# Revit family: Camera-Security-Vaddio-PTZ-RoboShot
name_source: partatom
category: Communication Devices
revit_build: Autodesk Revit 2015 (Build: 20140905_0730(x64)
units: mm (PartAtom-declared; Revit-internal decimal feet)

## types (105) — shared parameters
Date Modified = February 28, 2019
Default Elevation = 48 "
Description = See Part Description
Equipment Abbreviation = SC
Family Version = 1.0
Manufacturer = Vaddio
Model = See Part Number
Model Disclaimer = Contact Vaddio For More Information
Mount Material = Steel - Vaddio - White
Mount Trim Material = Plastic - Vaddio - White
Product Page URL = http://www.vaddio.com
URL = http://www.vaddio.com

## per-type parameters (varying)
| type | Camera Material | Camera Trim Material | Humidity | Image Sensor | Lens Type | Product Documentation Link | Resolution | Sales Region | Signal to Noise Ratio | Storage Temperature | Wide Dynamic Range | z Part Description | z Part Number | z Type Camera Series | z Type Mount Series |
| AVBMP, 12x Zoom, North America, Silver | Plastic - Vaddio - Silver | Plastic - Vaddio - Black | 20% to 80% Humidity | Exmor 1/2.8?, 2.34 Megapixel, Full HD (1080p/60 native) High-speed, Low Noise CMOS Image Sensor | 12X Optical Zoom with 73.0ø (wide end) to 6.6ø (tele end), f=3.91mm to 47mm, F1.8 to F3.4 | http://www.vaddio.com | 1080 x 1920 | North America | > 50 dB | 0øC to +40øC (32øF to 104øF) | No | Vaddio AVBMP, 12x Zoom, North America, Silver PTZ Camera | 999-9900-500 | 12 | 30 |
| AVBMP, 30x Zoom, North America, Black | Plastic - Vaddio - Black | Plastic - Vaddio - Black | 20% to 80% Humidity | Exmor 1/2.8?, 2.38 Megapixel, Full HD (1080p/60 native) High-speed, Low Noise CMOS Image Sensor | 30X Optical Zoom | http://www.vaddio.com | 1080 x 1920 | North America | > 50 dB | 0øC to +40øC (32øF to 104øF) | No | Vaddio AVBMP, 30x Zoom, North America, Black PTZ Camera | 999-9910-500 | 30 | 30 |
| AVBMP, 30x Zoom, North America, White | Plastic - Vaddio - White | Plastic - Vaddio - White | 20% to 80% Humidity | Exmor 1/2.8?, 2.38 Megapixel, Full HD (1080p/60 native) High-speed, Low Noise CMOS Image Sensor | 30X Optical Zoom | http://www.vaddio.com | 1080 x 1920 | North America | > 50 dB | 0øC to +40øC (32øF to 104øF) | No | Vaddio AVBMP, 30x Zoom, North America, White PTZ Camera | 999-9910-500W | 30 | 30 |
| AVBMP, 12x Zoom, North America, Elite, Black | Plastic - Vaddio - Black | Plastic - Vaddio - Black | 20% to 80% Humidity | Exmor 1/2.8?, 2.34 Megapixel, Full HD (1080p/60 native) High-speed, Low Noise CMOS Image Sensor | 12X Optical Zoom with 73.0ø (wide end) to 6.6ø (tele end), f=3.91mm to 47mm, F1.8 to F3.4 |  | 1080 x 1920 | North America | > 50 dB | 0øC to +40øC (32øF to 104øF) | No | Vaddio AVBMP, 12x Zoom, North America, Elite, Black PTZ Camera | 999-99000-500 | 12 | 30 |
| AVBMP, 12x Zoom, North America, Elite, White | Plastic - Vaddio - White | Plastic - Vaddio - White | 20% to 80% Humidity | Exmor 1/2.8?, 2.34 Megapixel, Full HD (1080p/60 native) High-speed, Low Noise CMOS Image Sensor | 12X Optical Zoom with 73.0ø (wide end) to 6.6ø (tele end), f=3.91mm to 47mm, F1.8 to F3.4 |  | 1080 x 1920 | North America | > 50 dB | 0øC to +40øC (32øF to 104øF) | No | Vaddio AVBMP, 12x Zoom, North America, Elite, White PTZ Camera | 999-99000-500W | 12 | 30 |
| AVBMP, 30x Zoom, North America, Elite, Black | Plastic - Vaddio - Black | Plastic - Vaddio - Black | 20% to 80% Humidity | Exmor 1/2.8?, 2.38 Megapixel, Full HD (1080p/60 native) High-speed, Low Noise CMOS Image Sensor | 30X Optical Zoom |  | 1080 x 1920 | North America | > 50 dB | 0øC to +40øC (32øF to 104øF) | No | Vaddio AVBMP, 30x Zoom, North America, Elite, Black PTZ Camera | 999-99100-500 | 30 | 30 |
| AVBMP, 30x Zoom, North America, Elite, White | Plastic - Vaddio - White | Plastic - Vaddio - White | 20% to 80% Humidity | Exmor 1/2.8?, 2.38 Megapixel, Full HD (1080p/60 native) High-speed, Low Noise CMOS Image Sensor | 30X Optical Zoom |  | 1080 x 1920 | North America | > 50 dB | 0øC to +40øC (32øF to 104øF) | No | Vaddio AVBMP, 30x Zoom, North America, Elite, White PTZ Camera | 999-99100-500W | 30 | 30 |
| HDBT, 30x Zoom, North America, Black | Plastic - Vaddio - Black | Plastic - Vaddio - Black | 20% to 80% RH, non-condensing | 1/2.8-Type Exmor R? backlit CMOS sensor | 30X optical zoom, 65ø (wide) to 2.3ø (tele), F1.6 to F4.7 | http://www.vaddio.com | 1080 x 1920 | North America | More than 50 dB | 0øC to +40øC (32øF to 104øF) | No | Vaddio HDBT, 30x Zoom, North America, Black PTZ Camera | 999-9963-000 | 30 | 30 |
| HDBT, 30x Zoom, North America, White | Plastic - Vaddio - White | Plastic - Vaddio - White | 20% to 80% RH, non-condensing | 1/2.8-Type Exmor R? backlit CMOS sensor | 30X optical zoom, 65ø (wide) to 2.3ø (tele), F1.6 to F4.7 | http://www.vaddio.com | 1080 x 1920 | North America | More than 50 dB | 0øC to +40øC (32øF to 104øF) | No | Vaddio HDBT, 30x Zoom, North America, White PTZ Camera | 999-9963-000W | 30 | 30 |
| HDBT, 30x Zoom, Europe/UK, Black | Plastic - Vaddio - Black | Plastic - Vaddio - Black | 20% to 80% RH, non-condensing | 1/2.8-Type Exmor R? backlit CMOS sensor | 30X optical zoom, 65ø (wide) to 2.3ø (tele), F1.6 to F4.7 | http://www.vaddio.com | 1080 x 1920 | Europe/UK | More than 50 dB | 0øC to +40øC (32øF to 104øF) | No | Vaddio HDBT, 30x Zoom, Europe/UK, Black PTZ Camera | 999-9963-001 | 30 | 30 |
| HDBT, 30x Zoom, Europe/UK, White | Plastic - Vaddio - White | Plastic - Vaddio - White | 20% to 80% RH, non-condensing | 1/2.8-Type Exmor R? backlit CMOS sensor | 30X optical zoom, 65ø (wide) to 2.3ø (tele), F1.6 to F4.7 | http://www.vaddio.com | 1080 x 1920 | Europe/UK | More than 50 dB | 0øC to +40øC (32øF to 104øF) | No | Vaddio HDBT, 30x Zoom, Europe/UK, White PTZ Camera | 999-9963-001W | 30 | 30 |
| HDBT, 30x Zoom, Australia/New Zealand, Black | Plastic - Vaddio - Black | Plastic - Vaddio - Black | 20% to 80% RH, non-condensing | 1/2.8-Type Exmor R? backlit CMOS sensor | 30X optical zoom, 65ø (wide) to 2.3ø (tele), F1.6 to F4.7 | http://www.vaddio.com | 1080 x 1920 | Australia/New Zealand | More than 50 dB | 0øC to +40øC (32øF to 104øF) | No | Vaddio HDBT, 30x Zoom, Australia/New Zealand, Black PTZ Camera | 999-9963-009 | 30 | 30 |
| HDBT, 30x Zoom, Australia/New Zealand, White | Plastic - Vaddio - White | Plastic - Vaddio - White | 20% to 80% RH, non-condensing | 1/2.8-Type Exmor R? backlit CMOS sensor | 30X optical zoom, 65ø (wide) to 2.3ø (tele), F1.6 to F4.7 | http://www.vaddio.com | 1080 x 1920 | Australia/New Zealand | More than 50 dB | 0øC to +40øC (32øF to 104øF) | No | Vaddio HDBT, 30x Zoom, Australia/New Zealand, White PTZ Camera | 999-9963-009W | 30 | 30 |
| HDBT, 12x Zoom, North America, Silver | Plastic - Vaddio - Silver | Plastic - Vaddio - Black | 20% to 80% RH, non-condensing | 1/2.8-Type Exmor? CMOS sensor | 12X optical zoom, 73.0ø (wide) to 6.6ø (tele), f=3.91mm to 47.0mm,ÿ F1.8 to F3.4 | http://www.vaddio.com | 1080 x 1920 | North America | More than 50 dB | 0øC to +40øC (32øF to 104øF) | No | Vaddio HDBT, 12x Zoom, North America, Silver PTZ Camera | 999-9960-000 | 12 | 30 |
| HDBT, 12x Zoom, Europe/UK, Silver | Plastic - Vaddio - Silver | Plastic - Vaddio - Black | 20% to 80% RH, non-condensing | 1/2.8-Type Exmor? CMOS sensor | 12X optical zoom, 73.0ø (wide) to 6.6ø (tele), f=3.91mm to 47.0mm,ÿ F1.8 to F3.4 | http://www.vaddio.com | 1080 x 1920 | Europe/UK | More than 50 dB | 0øC to +40øC (32øF to 104øF) | No | Vaddio HDBT, 12x Zoom, Europe/UK, Silver PTZ Camera | 999-9960-001 | 12 | 30 |
| HDBT, 12x Zoom, Australia/New Zealand, Silver | Plastic - Vaddio - Silver | Plastic - Vaddio - Black | 20% to 80% RH, non-condensing | 1/2.8-Type Exmor? CMOS sensor | 12X optical zoom, 73.0ø (wide) to 6.6ø (tele), f=3.91mm to 47.0mm,ÿ F1.8 to F3.4 | http://www.vaddio.com | 1080 x 1920 | Australia/New Zealand | More than 50 dB | 0øC to +40øC (32øF to 104øF) | No | Vaddio HDBT, 12x Zoom, Australia/New Zealand, Silver PTZ Camera | 999-9960-009 | 12 | 30 |
| HDBT, 12x Zoom, North America, Elite, Black | Plastic - Vaddio - Black | Plastic - Vaddio - Black | 20% to 80% RH, non-condensing | 1/2.5 Type Exmor R CMOS Sensor | 12x optical zoom, f=4.4mm wide end to 88.4mm tele end, F2 to F3.8 | http://www.vaddio.com | 1080 x 1920 | North America | More than 50 dB | 0øC to +40øC (32øF to 104øF) | Yes | Vaddio HDBT, 12x Zoom, North America, Elite, Black PTZ Camera | 999-99600-000 | 12 | 30 |
| HDBT, 12x Zoom, North America, Elite, White | Plastic - Vaddio - White | Plastic - Vaddio - White | 20% to 80% RH, non-condensing | 1/2.5 Type Exmor R CMOS Sensor | 12x optical zoom, f=4.4mm wide end to 88.4mm tele end, F2 to F3.8 | http://www.vaddio.com | 1080 x 1920 | North America | More than 50 dB | 0øC to +40øC (32øF to 104øF) | Yes | Vaddio HDBT, 12x Zoom, North America, Elite, White PTZ Camera | 999-99600-000W | 12 | 30 |
| HDBT, 30x Zoom, North America, Elite, Black | Plastic - Vaddio - Black | Plastic - Vaddio - Black | 20% to 80% RH, non-condensing | 1/2.5 Type Exmor R CMOS Sensor | 30x zoom, 20 x optical zoom + 10x IntelliZoom, f=4.4mm wide end to 88.4mm tele end, F2 to F3.8 | http://www.vaddio.com | 1080 x 1920 | North America | More than 50 dB | 0øC to +40øC (32øF to 104øF) | Yes | Vaddio HDBT, 30x Zoom, North America, Elite, Black PTZ Camera | 999-99630-000 | 30 | 30 |
| HDBT, 30x Zoom, North America, Elite, White | Plastic - Vaddio - White | Plastic - Vaddio - White | 20% to 80% RH, non-condensing | 1/2.5 Type Exmor R CMOS Sensor | 30x zoom, 20 x optical zoom + 10x IntelliZoom, f=4.4mm wide end to 88.4mm tele end, F2 to F3.8 | http://www.vaddio.com | 1080 x 1920 | North America | More than 50 dB | 0øC to +40øC (32øF to 104øF) | Yes | Vaddio HDBT, 30x Zoom, North America, Elite, White PTZ Camera | 999-99630-000W | 30 | 30 |
| HDBT, 12x Zoom, Europe/UK, Elite, Black | Plastic - Vaddio - Black | Plastic - Vaddio - Black | 20% to 80% RH, non-condensing | 1/2.5 Type Exmor R CMOS Sensor | 12x optical zoom, f=4.4mm wide end to 88.4mm tele end, F2 to F3.8 | http://www.vaddio.com | 1080 x 1920 | Europe/UK | More than 50 dB | 0øC to +40øC (32øF to 104øF) | Yes | Vaddio HDBT, 12x Zoom, Europe/UK, Elite, Black PTZ Camera | 999-99600-001 | 12 | 30 |
| HDBT, 12x Zoom, Europe/UK, Elite, White | Plastic - Vaddio - White | Plastic - Vaddio - White | 20% to 80% RH, non-condensing | 1/2.5 Type Exmor R CMOS Sensor | 12x optical zoom, f=4.4mm wide end to 88.4mm tele end, F2 to F3.8 | http://www.vaddio.com | 1080 x 1920 | Europe/UK | More than 50 dB | 0øC to +40øC (32øF to 104øF) | Yes | Vaddio HDBT, 12x Zoom, Europe/UK, Elite, White PTZ Camera | 999-99600-001W | 12 | 30 |
| HDBT, 30x Zoom, Europe/UK, Elite, Black | Plastic - Vaddio - Black | Plastic - Vaddio - Black | 20% to 80% RH, non-condensing | 1/2.5 Type Exmor R CMOS Sensor | 30x zoom, 20 x optical zoom + 10x IntelliZoom, f=4.4mm wide end to 88.4mm tele end, F2 to F3.8 | http://www.vaddio.com | 1080 x 1920 | Europe/UK | More than 50 dB | 0øC to +40øC (32øF to 104øF) | Yes | Vaddio HDBT, 30x Zoom, Europe/UK, Elite, Black PTZ Camera | 999-99630-001 | 30 | 30 |
| HDBT, 30x Zoom, Europe/UK, Elite, White | Plastic - Vaddio - White | Plastic - Vaddio - White | 20% to 80% RH, non-condensing | 1/2.5 Type Exmor R CMOS Sensor | 30x zoom, 20 x optical zoom + 10x IntelliZoom, f=4.4mm wide end to 88.4mm tele end, F2 to F3.8 | http://www.vaddio.com | 1080 x 1920 | Europe/UK | More than 50 dB | 0øC to +40øC (32øF to 104øF) | Yes | Vaddio HDBT, 30x Zoom, Europe/UK, Elite, White PTZ Camera | 999-99630-001W | 30 | 30 |
| HDBT, 12x Zoom, Australia/New Zealand, Elite, Black | Plastic - Vaddio - Black | Plastic - Vaddio - Black | 20% to 80% RH, non-condensing | 1/2.5 Type Exmor R CMOS Sensor | 12x optical zoom, f=4.4mm wide end to 88.4mm tele end, F2 to F3.8 | http://www.vaddio.com | 1080 x 1920 | Australia/New Zealand | More than 50 dB | 0øC to +40øC (32øF to 104øF) | Yes | Vaddio HDBT, 12x Zoom, Australia/New Zealand, Elite, Black PTZ Camera | 999-99600-009 | 12 | 30 |
| HDBT, 12x Zoom, Australia/New Zealand, Elite, White | Plastic - Vaddio - White | Plastic - Vaddio - White | 20% to 80% RH, non-condensing | 1/2.5 Type Exmor R CMOS Sensor | 12x optical zoom, f=4.4mm wide end to 88.4mm tele end, F2 to F3.8 | http://www.vaddio.com | 1080 x 1920 | Australia/New Zealand | More than 50 dB | 0øC to +40øC (32øF to 104øF) | Yes | Vaddio HDBT, 12x Zoom, Australia/New Zealand, Elite, White PTZ Camera | 999-99600-009W | 12 | 30 |
| HDBT, 30x Zoom, Australia/New Zealand, Elite, Black | Plastic - Vaddio - Black | Plastic - Vaddio - Black | 20% to 80% RH, non-condensing | 1/2.5 Type Exmor R CMOS Sensor | 30x zoom, 20 x optical zoom + 10x IntelliZoom, f=4.4mm wide end to 88.4mm tele end, F2 to F3.8 | http://www.vaddio.com | 1080 x 1920 | Australia/New Zealand | More than 50 dB | 0øC to +40øC (32øF to 104øF) | Yes | Vaddio HDBT, 30x Zoom, Australia/New Zealand, Elite, Black PTZ Camera | 999-99630-009 | 30 | 30 |
| HDBT, 30x Zoom, Australia/New Zealand, Elite, White | Plastic - Vaddio - White | Plastic - Vaddio - White | 20% to 80% RH, non-condensing | 1/2.5 Type Exmor R CMOS Sensor | 30x zoom, 20 x optical zoom + 10x IntelliZoom, f=4.4mm wide end to 88.4mm tele end, F2 to F3.8 | http://www.vaddio.com | 1080 x 1920 | Australia/New Zealand | More than 50 dB | 0øC to +40øC (32øF to 104øF) | Yes | Vaddio HDBT, 30x Zoom, Australia/New Zealand, Elite, White PTZ Camera | 999-99630-009W | 30 | 30 |
| HDMI, 30x Zoom, North America, Black | Plastic - Vaddio - Black | Plastic - Vaddio - Black | 20% to 80% Humidity | Exmor 1/2.8?, 2.38 Megapixels, Full HD (1080p/60 native) High-speed, Low Noise CMOS Image Sensor | 65ø wide end to 2.3ø tele end, f=4.3mm to 129mm, F1.6 to F4.7 | http://www.vaddio.com | 1080 x 1920 | North America | > 50 dB | 0øC to +40øC (32øF to 104øF) | No | Vaddio HDMI, 30x Zoom, North America, Black PTZ Camera | 999-9943-000 | 30 | 30 |
| HDMI, 30x Zoom, North America, White | Plastic - Vaddio - White | Plastic - Vaddio - White | 20% to 80% Humidity | Exmor 1/2.8?, 2.38 Megapixels, Full HD (1080p/60 native) High-speed, Low Noise CMOS Image Sensor | 65ø wide end to 2.3ø tele end, f=4.3mm to 129mm, F1.6 to F4.7 | http://www.vaddio.com | 1080 x 1920 | North America | > 50 dB | 0øC to +40øC (32øF to 104øF) | No | Vaddio HDMI, 30x Zoom, North America, White PTZ Camera | 999-9943-000W | 30 | 30 |
| HDMI, 30x Zoom, Europe/UK, Black | Plastic - Vaddio - Black | Plastic - Vaddio - Black | 20% to 80% Humidity | Exmor 1/2.8?, 2.38 Megapixels, Full HD (1080p/60 native) High-speed, Low Noise CMOS Image Sensor | 65ø wide end to 2.3ø tele end, f=4.3mm to 129mm, F1.6 to F4.7 | http://www.vaddio.com | 1080 x 1920 | Europe/UK | > 50 dB | 0øC to +40øC (32øF to 104øF) | No | Vaddio HDMI, 30x Zoom, Europe/UK, Black PTZ Camera | 999-9943-001 | 30 | 30 |
| HDMI, 30x Zoom, Europe/UK, White | Plastic - Vaddio - White | Plastic - Vaddio - White | 20% to 80% Humidity | Exmor 1/2.8?, 2.38 Megapixels, Full HD (1080p/60 native) High-speed, Low Noise CMOS Image Sensor | 65ø wide end to 2.3ø tele end, f=4.3mm to 129mm, F1.6 to F4.7 | http://www.vaddio.com | 1080 x 1920 | Europe/UK | > 50 dB | 0øC to +40øC (32øF to 104øF) | No | Vaddio HDMI, 30x Zoom, Europe/UK, White PTZ Camera | 999-9943-001W | 30 | 30 |
| HDMI, 12x Zoom, North America, Cisco SX Codecs, Silver | Plastic - Vaddio - Silver | Plastic - Vaddio - Black | 20% to 80% Humidity | Exmor 1/2.8?, 2.38 Megapixels, Full HD (1080p/60 native) High-speed, Low Noise CMOS Image Sensor | 12X Mode: f=3.91mm to 47.0mm, F1.8 to F3.4 | http://www.vaddio.com | 1080 x 1920 | North America | > 50 dB | 0øC to +40øC (32øF to 104øF) | No | Vaddio HDMI, 12x Zoom, North America, Cisco SX Codecs, Silver PTZ Camera | 999-9940-400 | 12 | 30 |
| HDMI, 12x Zoom, North America, Polycom Codecs, Silver | Plastic - Vaddio - Silver | Plastic - Vaddio - Black | 20% to 80% Humidity | Exmor 1/2.8?, 2.38 Megapixels, Full HD (1080p/60 native) High-speed, Low Noise CMOS Image Sensor | 12X Mode: f=3.91mm to 47.0mm, F1.8 to F3.4 | http://www.vaddio.com | 1080 x 1920 | North America | > 50 dB | 0øC to +40øC (32øF to 104øF) | No | Vaddio HDMI, 12x Zoom, North America, Polycom Codecs, Silver PTZ Camera | 999-9940-500 | 12 | 30 |
| HDMI, 12x Zoom, North America, Silver | Plastic - Vaddio - Silver | Plastic - Vaddio - Black | 20% to 80% Humidity | Exmor 1/2.8?, 2.38 Megapixels, Full HD (1080p/60 native) High-speed, Low Noise CMOS Image Sensor | 12X Mode: f=3.91mm to 47.0mm, F1.8 to F3.4 | http://www.vaddio.com | 1080 x 1920 | North America | > 50 dB | 0øC to +40øC (32øF to 104øF) | No | Vaddio HDMI, 12x Zoom, North America, Silver PTZ Camera | 999-9940-000 | 12 | 30 |
| HDMI, 12x Zoom, Europe/UK, Cisco SX Codecs, Silver | Plastic - Vaddio - Silver | Plastic - Vaddio - Black | 20% to 80% Humidity | Exmor 1/2.8?, 2.38 Megapixels, Full HD (1080p/60 native) High-speed, Low Noise CMOS Image Sensor | 12X Mode: f=3.91mm to 47.0mm, F1.8 to F3.4 | http://www.vaddio.com | 1080 x 1920 | Europe/UK | > 50 dB | 0øC to +40øC (32øF to 104øF) | No | Vaddio HDMI, 12x Zoom, Europe/UK, Cisco SX Codecs, Silver PTZ Camera | 999-9940-401 | 12 | 30 |
| HDMI, 12x Zoom, Europe/UK, Polycom Codecs, Silver | Plastic - Vaddio - Silver | Plastic - Vaddio - Black | 20% to 80% Humidity | Exmor 1/2.8?, 2.38 Megapixels, Full HD (1080p/60 native) High-speed, Low Noise CMOS Image Sensor | 12X Mode: f=3.91mm to 47.0mm, F1.8 to F3.4 | http://www.vaddio.com | 1080 x 1920 | Europe/UK | > 50 dB | 0øC to +40øC (32øF to 104øF) | No | Vaddio HDMI, 12x Zoom, Europe/UK, Polycom Codecs, Silver PTZ Camera | 999-9940-501 | 12 | 30 |
| HDMI, 12x Zoom, Europe/UK, Silver | Plastic - Vaddio - Silver | Plastic - Vaddio - Black | 20% to 80% Humidity | Exmor 1/2.8?, 2.38 Megapixels, Full HD (1080p/60 native) High-speed, Low Noise CMOS Image Sensor | 12X Mode: f=3.91mm to 47.0mm, F1.8 to F3.4 | http://www.vaddio.com | 1080 x 1920 | Europe/UK | > 50 dB | 0øC to +40øC (32øF to 104øF) | No | Vaddio HDMI, 12x Zoom, Europe/UK, Silver PTZ Camera | 999-9940-001 | 12 | 30 |
| HDMI, 12x Zoom, Australia/New Zealand, Silver | Plastic - Vaddio - Silver | Plastic - Vaddio - Black | 20% to 80% Humidity | Exmor 1/2.8?, 2.38 Megapixels, Full HD (1080p/60 native) High-speed, Low Noise CMOS Image Sensor | 12X Mode: f=3.91mm to 47.0mm, F1.8 to F3.4 | http://www.vaddio.com | 1080 x 1920 | Australia/New Zealand | > 50 dB | 0øC to +40øC (32øF to 104øF) | No | Vaddio HDMI, 12x Zoom, Australia/New Zealand, Silver PTZ Camera | 999-9940-009 | 12 | 30 |
| HDMI, 12x Zoom, North America, Elite, Cisco SX Codecs, Black | Plastic - Vaddio - Black | Plastic - Vaddio - Black | 20% to 80% Humidity | Exmor 1/2.8?, 2.38 Megapixels, Full HD (1080p/60 native) High-speed, Low Noise CMOS Image Sensor | 12X Mode: f=3.91mm to 47.0mm, F1.8 to F3.4 |  | 1080 x 1920 | North America | > 50 dB | 0øC to +40øC (32øF to 104øF) | No | Vaddio HDMI, 12x Zoom, North America, Elite, Cisco SX Codecs, Black PTZ Camera | 999-99400-400 | 12 | 30 |
| HDMI, 12x Zoom, North America, Elite, Cisco SX Codecs, White | Plastic - Vaddio - White | Plastic - Vaddio - White | 20% to 80% Humidity | Exmor 1/2.8?, 2.38 Megapixels, Full HD (1080p/60 native) High-speed, Low Noise CMOS Image Sensor | 12X Mode: f=3.91mm to 47.0mm, F1.8 to F3.4 |  | 1080 x 1920 | North America | > 50 dB | 0øC to +40øC (32øF to 104øF) | No | Vaddio HDMI, 12x Zoom, North America, Elite, Cisco SX Codecs, White PTZ Camera | 999-99400-400W | 12 | 30 |
| HDMI, 12x Zoom, North America, Elite, Polycom Codecs, Black | Plastic - Vaddio - Black | Plastic - Vaddio - Black | 20% to 80% Humidity | Exmor 1/2.8?, 2.38 Megapixels, Full HD (1080p/60 native) High-speed, Low Noise CMOS Image Sensor | 12X Mode: f=3.91mm to 47.0mm, F1.8 to F3.4 |  | 1080 x 1920 | North America | > 50 dB | 0øC to +40øC (32øF to 104øF) | No | Vaddio HDMI, 12x Zoom, North America, Elite, Polycom Codecs, Black PTZ Camera | 999-99400-500 | 12 | 30 |
| HDMI, 12x Zoom, North America, Elite, Polycom Codecs, White | Plastic - Vaddio - White | Plastic - Vaddio - White | 20% to 80% Humidity | Exmor 1/2.8?, 2.38 Megapixels, Full HD (1080p/60 native) High-speed, Low Noise CMOS Image Sensor | 12X Mode: f=3.91mm to 47.0mm, F1.8 to F3.4 |  | 1080 x 1920 | North America | > 50 dB | 0øC to +40øC (32øF to 104øF) | No | Vaddio HDMI, 12x Zoom, North America, Elite, Polycom Codecs, White PTZ Camera | 999-99400-500W | 12 | 30 |
| HDMI, 12x Zoom, North America, Black | Plastic - Vaddio - Black | Plastic - Vaddio - Black | 20% to 80% Humidity | Exmor 1/2.8?, 2.38 Megapixels, Full HD (1080p/60 native) High-speed, Low Noise CMOS Image Sensor | 12X Mode: f=3.91mm to 47.0mm, F1.8 to F3.4 |  | 1080 x 1920 | North America | > 50 dB | 0øC to +40øC (32øF to 104øF) | No | Vaddio HDMI, 12x Zoom, North America, Black PTZ Camera | 999-99400-000 | 12 | 30 |
| HDMI, 12x Zoom, North America, White | Plastic - Vaddio - White | Plastic - Vaddio - White | 20% to 80% Humidity | Exmor 1/2.8?, 2.38 Megapixels, Full HD (1080p/60 native) High-speed, Low Noise CMOS Image Sensor | 12X Mode: f=3.91mm to 47.0mm, F1.8 to F3.4 |  | 1080 x 1920 | North America | > 50 dB | 0øC to +40øC (32øF to 104øF) | No | Vaddio HDMI, 12x Zoom, North America, White PTZ Camera | 999-99400-000W | 12 | 30 |
| HDMI, 30x Zoom, North America, Elite, Black | Plastic - Vaddio - Black | Plastic - Vaddio - Black | 20% to 80% Humidity | Exmor 1/2.8?, 2.38 Megapixels, Full HD (1080p/60 native) High-speed, Low Noise CMOS Image Sensor | 65ø wide end to 2.3ø tele end, f=4.3mm to 129mm, F1.6 to F4.7 |  | 1080 x 1920 | North America | > 50 dB | 0øC to +40øC (32øF to 104øF) | No | Vaddio HDMI, 30x Zoom, North America, Elite, Black PTZ Camera | 999-99430-000 | 30 | 30 |
| HDMI, 30x Zoom, North America, Elite, White | Plastic - Vaddio - White | Plastic - Vaddio - White | 20% to 80% Humidity | Exmor 1/2.8?, 2.38 Megapixels, Full HD (1080p/60 native) High-speed, Low Noise CMOS Image Sensor | 65ø wide end to 2.3ø tele end, f=4.3mm to 129mm, F1.6 to F4.7 |  | 1080 x 1920 | North America | > 50 dB | 0øC to +40øC (32øF to 104øF) | No | Vaddio HDMI, 30x Zoom, North America, Elite, White PTZ Camera | 999-99430-000W | 30 | 30 |
| HDMI, 12x Zoom, Europe/UK, Elite, Cisco SX Codecs, Black | Plastic - Vaddio - Black | Plastic - Vaddio - Black | 20% to 80% Humidity | Exmor 1/2.8?, 2.38 Megapixels, Full HD (1080p/60 native) High-speed, Low Noise CMOS Image Sensor | 12X Mode: f=3.91mm to 47.0mm, F1.8 to F3.4 |  | 1080 x 1920 | Europe/UK | > 50 dB | 0øC to +40øC (32øF to 104øF) | No | Vaddio HDMI, 12x Zoom, Europe/UK, Elite, Cisco SX Codecs, Black PTZ Camera | 999-99400-401 | 12 | 30 |
| HDMI, 12x Zoom, Europe/UK, Elite, Cisco SX Codecs, White | Plastic - Vaddio - White | Plastic - Vaddio - White | 20% to 80% Humidity | Exmor 1/2.8?, 2.38 Megapixels, Full HD (1080p/60 native) High-speed, Low Noise CMOS Image Sensor | 12X Mode: f=3.91mm to 47.0mm, F1.8 to F3.4 |  | 1080 x 1920 | Europe/UK | > 50 dB | 0øC to +40øC (32øF to 104øF) | No | Vaddio HDMI, 12x Zoom, Europe/UK, Elite, Cisco SX Codecs, White PTZ Camera | 999-99400-401W | 12 | 30 |
| HDMI, 12x Zoom, Europe/UK, Elite, Polycom Codecs, Black | Plastic - Vaddio - Black | Plastic - Vaddio - Black | 20% to 80% Humidity | Exmor 1/2.8?, 2.38 Megapixels, Full HD (1080p/60 native) High-speed, Low Noise CMOS Image Sensor | 12X Mode: f=3.91mm to 47.0mm, F1.8 to F3.4 |  | 1080 x 1920 | Europe/UK | > 50 dB | 0øC to +40øC (32øF to 104øF) | No | Vaddio HDMI, 12x Zoom, Europe/UK, Elite, Polycom Codecs, Black PTZ Camera | 999-99400-501 | 12 | 30 |
| HDMI, 12x Zoom, Europe/UK, Elite, Polycom Codecs, White | Plastic - Vaddio - White | Plastic - Vaddio - White | 20% to 80% Humidity | Exmor 1/2.8?, 2.38 Megapixels, Full HD (1080p/60 native) High-speed, Low Noise CMOS Image Sensor | 12X Mode: f=3.91mm to 47.0mm, F1.8 to F3.4 |  | 1080 x 1920 | Europe/UK | > 50 dB | 0øC to +40øC (32øF to 104øF) | No | Vaddio HDMI, 12x Zoom, Europe/UK, Elite, Polycom Codecs, White PTZ Camera | 999-99400-501W | 12 | 30 |
| HDMI, 12x Zoom, Europe/UK, Black | Plastic - Vaddio - Black | Plastic - Vaddio - Black | 20% to 80% Humidity | Exmor 1/2.8?, 2.38 Megapixels, Full HD (1080p/60 native) High-speed, Low Noise CMOS Image Sensor | 12X Mode: f=3.91mm to 47.0mm, F1.8 to F3.4 |  | 1080 x 1920 | Europe/UK | > 50 dB | 0øC to +40øC (32øF to 104øF) | No | Vaddio HDMI, 12x Zoom, Europe/UK, Black PTZ Camera | 999-99400-001 | 12 | 30 |
| HDMI, 12x Zoom, Europe/UK, White | Plastic - Vaddio - White | Plastic - Vaddio - White | 20% to 80% Humidity | Exmor 1/2.8?, 2.38 Megapixels, Full HD (1080p/60 native) High-speed, Low Noise CMOS Image Sensor | 12X Mode: f=3.91mm to 47.0mm, F1.8 to F3.4 |  | 1080 x 1920 | Europe/UK | > 50 dB | 0øC to +40øC (32øF to 104øF) | No | Vaddio HDMI, 12x Zoom, Europe/UK, White PTZ Camera | 999-99400-001W | 12 | 30 |
| HDMI, 30x Zoom, Europe/UK, Elite, Black | Plastic - Vaddio - Black | Plastic - Vaddio - Black | 20% to 80% Humidity | Exmor 1/2.8?, 2.38 Megapixels, Full HD (1080p/60 native) High-speed, Low Noise CMOS Image Sensor | 65ø wide end to 2.3ø tele end, f=4.3mm to 129mm, F1.6 to F4.7 |  | 1080 x 1920 | Europe/UK | > 50 dB | 0øC to +40øC (32øF to 104øF) | No | Vaddio HDMI, 30x Zoom, Europe/UK, Elite, Black PTZ Camera | 999-99430-001 | 30 | 30 |
| HDMI, 30x Zoom, Europe/UK, Elite, White | Plastic - Vaddio - White | Plastic - Vaddio - White | 20% to 80% Humidity | Exmor 1/2.8?, 2.38 Megapixels, Full HD (1080p/60 native) High-speed, Low Noise CMOS Image Sensor | 65ø wide end to 2.3ø tele end, f=4.3mm to 129mm, F1.6 to F4.7 |  | 1080 x 1920 | Europe/UK | > 50 dB | 0øC to +40øC (32øF to 104øF) | No | Vaddio HDMI, 30x Zoom, Europe/UK, Elite, White PTZ Camera | 999-99430-001W | 30 | 30 |
| HDMI, 12x Zoom, Australia/New Zealand, Elite, Black | Plastic - Vaddio - Black | Plastic - Vaddio - Black | 20% to 80% Humidity | Exmor 1/2.8?, 2.38 Megapixels, Full HD (1080p/60 native) High-speed, Low Noise CMOS Image Sensor | 12X Mode: f=3.91mm to 47.0mm, F1.8 to F3.4 |  | 1080 x 1920 | Australia/New Zealand | > 50 dB | 0øC to +40øC (32øF to 104øF) | No | Vaddio HDMI, 12x Zoom, Australia/New Zealand, Elite, Black PTZ Camera | 999-99400-009 | 12 | 30 |
| HDMI, 12x Zoom, Australia/New Zealand, Elite, White | Plastic - Vaddio - White | Plastic - Vaddio - White | 20% to 80% Humidity | Exmor 1/2.8?, 2.38 Megapixels, Full HD (1080p/60 native) High-speed, Low Noise CMOS Image Sensor | 12X Mode: f=3.91mm to 47.0mm, F1.8 to F3.4 |  | 1080 x 1920 | Australia/New Zealand | > 50 dB | 0øC to +40øC (32øF to 104øF) | No | Vaddio HDMI, 12x Zoom, Australia/New Zealand, Elite, White PTZ Camera | 999-99400-009W | 12 | 30 |
| HD-SDI, 12x Zoom, North America, Silver | Plastic - Vaddio - Silver | Plastic - Vaddio - Black | 20% to 80% Relative Humidity | 1/2.8-Type Exmor CMOS sensor | 12X Optical Zoom, 73.0ø (wide) to 6.6ø (tele),f=3.91mm to 47.0mm, F1.8 to F3.4 | http://www.vaddio.com | 1080 x 1920 | North America | Greater than 50 dB | 0øC to +40øC (32øF to 104øF) | No | Vaddio HD-SDI, 12x Zoom, North America, Silver PTZ Camera | 999-9930-000 | 12 | 30 |
| HD-SDI, 30x Zoom, North America, Black | Plastic - Vaddio - Black | Plastic - Vaddio - Black | 20% to 80% Relative Humidity | 1/2.8-Type Exmor CMOS sensor | 30X optical zoom, 65ø (wide end) to 2.3ø (tele end), F1.6 to F4.7 | http://www.vaddio.com | 1080 x 1920 | North America | Greater than 50 dB | 0øC to +40øC (32øF to 104øF) | No | Vaddio HD-SDI, 30x Zoom, North America, Black PTZ Camera | 999-9933-000 | 30 | 30 |
| HD-SDI, 30x Zoom, North America, White | Plastic - Vaddio - White | Plastic - Vaddio - White | 20% to 80% Relative Humidity | 1/2.8-Type Exmor CMOS sensor | 30X optical zoom, 65ø (wide end) to 2.3ø (tele end), F1.6 to F4.7 | http://www.vaddio.com | 1080 x 1920 | North America | Greater than 50 dB | 0øC to +40øC (32øF to 104øF) | No | Vaddio HD-SDI, 30x Zoom, North America, White PTZ Camera | 999-9933-000W | 30 | 30 |
| HD-SDI, 12x Zoom, Europe/UK, Silver | Plastic - Vaddio - Silver | Plastic - Vaddio - Black | 20% to 80% Relative Humidity | 1/2.8-Type Exmor CMOS sensor | 12X Optical Zoom, 73.0ø (wide) to 6.6ø (tele),f=3.91mm to 47.0mm, F1.8 to F3.4 | http://www.vaddio.com | 1080 x 1920 | Europe/UK | Greater than 50 dB | 0øC to +40øC (32øF to 104øF) | No | Vaddio HD-SDI, 12x Zoom, Europe/UK, Silver PTZ Camera | 999-9930-001 | 12 | 30 |
| HD-SDI, 30x Zoom, Europe/UK, Black | Plastic - Vaddio - Black | Plastic - Vaddio - Black | 20% to 80% Relative Humidity | 1/2.8-Type Exmor CMOS sensor | 30X optical zoom, 65ø (wide end) to 2.3ø (tele end), F1.6 to F4.7 | http://www.vaddio.com | 1080 x 1920 | Europe/UK | Greater than 50 dB | 0øC to +40øC (32øF to 104øF) | No | Vaddio HD-SDI, 30x Zoom, Europe/UK, Black PTZ Camera | 999-9933-001 | 30 | 30 |
| HD-SDI, 30x Zoom, Europe/UK, White | Plastic - Vaddio - White | Plastic - Vaddio - White | 20% to 80% Relative Humidity | 1/2.8-Type Exmor CMOS sensor | 30X optical zoom, 65ø (wide end) to 2.3ø (tele end), F1.6 to F4.7 | http://www.vaddio.com | 1080 x 1920 | Europe/UK | Greater than 50 dB | 0øC to +40øC (32øF to 104øF) | No | Vaddio HD-SDI, 30x Zoom, Europe/UK, White PTZ Camera | 999-9933-001W | 30 | 30 |
| HD-SDI, 12x Zoom, Australia/New Zealand, Silver | Plastic - Vaddio - Silver | Plastic - Vaddio - Black | 20% to 80% Relative Humidity | 1/2.8-Type Exmor CMOS sensor | 12X Optical Zoom, 73.0ø (wide) to 6.6ø (tele),f=3.91mm to 47.0mm, F1.8 to F3.4 | http://www.vaddio.com | 1080 x 1920 | Australia/New Zealand | Greater than 50 dB | 0øC to +40øC (32øF to 104øF) | No | Vaddio HD-SDI, 12x Zoom, Australia/New Zealand, Silver PTZ Camera | 999-9930-009 | 12 | 30 |
| HD-SDI, 30x Zoom, Australia/New Zealand, Black | Plastic - Vaddio - Black | Plastic - Vaddio - Black | 20% to 80% Relative Humidity | 1/2.8-Type Exmor CMOS sensor | 30X optical zoom, 65ø (wide end) to 2.3ø (tele end), F1.6 to F4.7 | http://www.vaddio.com | 1080 x 1920 | Australia/New Zealand | Greater than 50 dB | 0øC to +40øC (32øF to 104øF) | No | Vaddio HD-SDI, 30x Zoom, Australia/New Zealand, Black PTZ Camera | 999-9933-009 | 30 | 30 |
| HD-SDI, 30x Zoom, Australia/New Zealand, White | Plastic - Vaddio - White | Plastic - Vaddio - White | 20% to 80% Relative Humidity | 1/2.8-Type Exmor CMOS sensor | 30X optical zoom, 65ø (wide end) to 2.3ø (tele end), F1.6 to F4.7 | http://www.vaddio.com | 1080 x 1920 | Australia/New Zealand | Greater than 50 dB | 0øC to +40øC (32øF to 104øF) | No | Vaddio HD-SDI, 30x Zoom, Australia/New Zealand, White PTZ Camera | 999-9933-009W | 30 | 30 |
| SDI, 30x Zoom, North America, Elite, Black | Plastic - Vaddio - Black | Plastic - Vaddio - Black | 20% to 80% Relative Humidity | 1/2.8-Type Exmor CMOS sensor | 30X optical zoom, 65ø (wide end) to 2.3ø (tele end), F1.6 to F4.7 |  | 1080 x 1920 | North America | Greater than 50 dB | 0øC to +40øC (32øF to 104øF) | No | Vaddio SDI, 30x Zoom, North America, Elite, Black PTZ Camera | 999-99330-000 | 30 | 30 |
| SDI, 30x Zoom, North America, Elite, White | Plastic - Vaddio - White | Plastic - Vaddio - White | 20% to 80% Relative Humidity | 1/2.8-Type Exmor CMOS sensor | 30X optical zoom, 65ø (wide end) to 2.3ø (tele end), F1.6 to F4.7 |  | 1080 x 1920 | North America | Greater than 50 dB | 0øC to +40øC (32øF to 104øF) | No | Vaddio SDI, 30x Zoom, North America, Elite, White PTZ Camera | 999-99330-000W | 30 | 30 |
| SDI, 30x Zoom, Europe/UK, Elite, Black | Plastic - Vaddio - Black | Plastic - Vaddio - Black | 20% to 80% Relative Humidity | 1/2.8-Type Exmor CMOS sensor | 30X optical zoom, 65ø (wide end) to 2.3ø (tele end), F1.6 to F4.7 |  | 1080 x 1920 | Europe/UK | Greater than 50 dB | 0øC to +40øC (32øF to 104øF) | No | Vaddio SDI, 30x Zoom, Europe/UK, Elite, Black PTZ Camera | 999-99330-001 | 30 | 30 |
| SDI, 30x Zoom, Europe/UK, Elite, White | Plastic - Vaddio - White | Plastic - Vaddio - White | 20% to 80% Relative Humidity | 1/2.8-Type Exmor CMOS sensor | 30X optical zoom, 65ø (wide end) to 2.3ø (tele end), F1.6 to F4.7 |  | 1080 x 1920 | Europe/UK | Greater than 50 dB | 0øC to +40øC (32øF to 104øF) | No | Vaddio SDI, 30x Zoom, Europe/UK, Elite, White PTZ Camera | 999-99330-001W | 30 | 30 |
| SDI, 30x Zoom, Australia/New Zealand, Elite, Black | Plastic - Vaddio - Black | Plastic - Vaddio - Black | 20% to 80% Relative Humidity | 1/2.8-Type Exmor CMOS sensor | 30X optical zoom, 65ø (wide end) to 2.3ø (tele end), F1.6 to F4.7 |  | 1080 x 1920 | Australia/New Zealand | Greater than 50 dB | 0øC to +40øC (32øF to 104øF) | No | Vaddio SDI, 30x Zoom, Australia/New Zealand, Elite, Black PTZ Camera | 999-99330-009 | 30 | 30 |
| SDI, 30x Zoom, Australia/New Zealand, Elite, White | Plastic - Vaddio - White | Plastic - Vaddio - White | 20% to 80% Relative Humidity | 1/2.8-Type Exmor CMOS sensor | 30X optical zoom, 65ø (wide end) to 2.3ø (tele end), F1.6 to F4.7 |  | 1080 x 1920 | Australia/New Zealand | Greater than 50 dB | 0øC to +40øC (32øF to 104øF) | No | Vaddio SDI, 30x Zoom, Australia/New Zealand, Elite, White PTZ Camera | 999-99330-009W | 30 | 30 |
| SDI, 12x Zoom, North America, Elite, Black | Plastic - Vaddio - Black | Plastic - Vaddio - Black | 20% to 80% Relative Humidity | 1/2.8-Type Exmor CMOS sensor | 12X Optical Zoom, 73.0ø (wide) to 6.6ø (tele),f=3.91mm to 47.0mm, F1.8 to F3.4 |  | 1080 x 1920 | North America | Greater than 50 dB | 0øC to +40øC (32øF to 104øF) | No | Vaddio SDI, 12x Zoom, North America, Elite, Black PTZ Camera | 999-99300-000 | 12 | 30 |
| SDI, 12x Zoom, North America, Elite, White | Plastic - Vaddio - White | Plastic - Vaddio - White | 20% to 80% Relative Humidity | 1/2.8-Type Exmor CMOS sensor | 12X Optical Zoom, 73.0ø (wide) to 6.6ø (tele),f=3.91mm to 47.0mm, F1.8 to F3.4 |  | 1080 x 1920 | North America | Greater than 50 dB | 0øC to +40øC (32øF to 104øF) | No | Vaddio SDI, 12x Zoom, North America, Elite, White PTZ Camera | 999-99300-000W | 12 | 30 |
| SDI, 12x Zoom, Europe/UK, Elite, Black | Plastic - Vaddio - Black | Plastic - Vaddio - Black | 20% to 80% Relative Humidity | 1/2.8-Type Exmor CMOS sensor | 12X Optical Zoom, 73.0ø (wide) to 6.6ø (tele),f=3.91mm to 47.0mm, F1.8 to F3.4 |  | 1080 x 1920 | Europe/UK | Greater than 50 dB | 0øC to +40øC (32øF to 104øF) | No | Vaddio SDI, 12x Zoom, Europe/UK, Elite, Black PTZ Camera | 999-99300-001 | 12 | 30 |
| SDI, 12x Zoom, Europe/UK, Elite, White | Plastic - Vaddio - White | Plastic - Vaddio - White | 20% to 80% Relative Humidity | 1/2.8-Type Exmor CMOS sensor | 12X Optical Zoom, 73.0ø (wide) to 6.6ø (tele),f=3.91mm to 47.0mm, F1.8 to F3.4 |  | 1080 x 1920 | Europe/UK | Greater than 50 dB | 0øC to +40øC (32øF to 104øF) | No | Vaddio SDI, 12x Zoom, Europe/UK, Elite, White PTZ Camera | 999-99300-001W | 12 | 30 |
| SDI, 12x Zoom, Australia/New Zealand, Elite, Black | Plastic - Vaddio - Black | Plastic - Vaddio - Black | 20% to 80% Relative Humidity | 1/2.8-Type Exmor CMOS sensor | 12X Optical Zoom, 73.0ø (wide) to 6.6ø (tele),f=3.91mm to 47.0mm, F1.8 to F3.4 |  | 1080 x 1920 | Australia/New Zealand | Greater than 50 dB | 0øC to +40øC (32øF to 104øF) | No | Vaddio SDI, 12x Zoom, Australia/New Zealand, Elite, Black PTZ Camera | 999-99300-009 | 12 | 30 |
| SDI, 12x Zoom, Australia/New Zealand, Elite, White | Plastic - Vaddio - White | Plastic - Vaddio - White | 20% to 80% Relative Humidity | 1/2.8-Type Exmor CMOS sensor | 12X Optical Zoom, 73.0ø (wide) to 6.6ø (tele),f=3.91mm to 47.0mm, F1.8 to F3.4 |  | 1080 x 1920 | Australia/New Zealand | Greater than 50 dB | 0øC to +40øC (32øF to 104øF) | No | Vaddio SDI, 12x Zoom, Australia/New Zealand, Elite, White PTZ Camera | 999-99300-009W | 12 | 30 |
| UHD, 40x Zoom, North America, Black | Plastic - Vaddio - Black | Plastic - Vaddio - Black | 20% to 80% RH, non-condensing | 1/2.5 Type Exmor R CMOS Sensor, 4K | 20x optical zoom, f=4.4mm wide end to 88.4mm tele end, F2 to F3.8 | http://www.vaddio.com | 3840 x 2160 | North America | More than 50 dB | 0øC to +40øC (32øF to 104øF) | Yes | Vaddio UHD, 40x Zoom, North America, Black PTZ Camera | 999-9952-000 | 40 | 20 |
| UHD, 40x Zoom, North America, White | Plastic - Vaddio - White | Plastic - Vaddio - White | 20% to 80% RH, non-condensing | 1/2.5 Type Exmor R CMOS Sensor, 4K | 20x optical zoom, f=4.4mm wide end to 88.4mm tele end, F2 to F3.8 | http://www.vaddio.com | 3840 x 2160 | North America | More than 50 dB | 0øC to +40øC (32øF to 104øF) | Yes | Vaddio UHD, 40x Zoom, North America, White PTZ Camera | 999-9952-000W | 40 | 20 |
| UHD, 40x Zoom, Europe/UK, Black | Plastic - Vaddio - Black | Plastic - Vaddio - Black | 20% to 80% RH, non-condensing | 1/2.5 Type Exmor R CMOS Sensor, 4K | 20x optical zoom, f=4.4mm wide end to 88.4mm tele end, F2 to F3.8 | http://www.vaddio.com | 3840 x 2160 | Europe/UK | More than 50 dB | 0øC to +40øC (32øF to 104øF) | Yes | Vaddio UHD, 40x Zoom, Europe/UK, Black PTZ Camera | 999-9952-001 | 40 | 20 |
| UHD, 40x Zoom, Europe/UK, White | Plastic - Vaddio - White | Plastic - Vaddio - White | 20% to 80% RH, non-condensing | 1/2.5 Type Exmor R CMOS Sensor, 4K | 20x optical zoom, f=4.4mm wide end to 88.4mm tele end, F2 to F3.8 | http://www.vaddio.com | 3840 x 2160 | Europe/UK | More than 50 dB | 0øC to +40øC (32øF to 104øF) | Yes | Vaddio UHD, 40x Zoom, Europe/UK, White PTZ Camera | 999-9952-001W | 40 | 20 |
| UHD, 40x Zoom, Australia/New Zealand, Black | Plastic - Vaddio - Black | Plastic - Vaddio - Black | 20% to 80% RH, non-condensing | 1/2.5 Type Exmor R CMOS Sensor, 4K | 20x optical zoom, f=4.4mm wide end to 88.4mm tele end, F2 to F3.8 | http://www.vaddio.com | 3840 x 2160 | Australia/New Zealand | More than 50 dB | 0øC to +40øC (32øF to 104øF) | Yes | Vaddio UHD, 40x Zoom, Australia/New Zealand, Black PTZ Camera | 999-9952-009 | 40 | 20 |
| UHD, 40x Zoom, Australia/New Zealand, White | Plastic - Vaddio - White | Plastic - Vaddio - White | 20% to 80% RH, non-condensing | 1/2.5 Type Exmor R CMOS Sensor, 4K | 20x optical zoom, f=4.4mm wide end to 88.4mm tele end, F2 to F3.8 | http://www.vaddio.com | 3840 x 2160 | Australia/New Zealand | More than 50 dB | 0øC to +40øC (32øF to 104øF) | Yes | Vaddio UHD, 40x Zoom, Australia/New Zealand, White PTZ Camera | 999-9952-009W | 40 | 20 |
| UHD, 20x Zoom, North America, Silver | Plastic - Vaddio - Silver | Plastic - Vaddio - Black | 20% to 80% RH (non-condensing) | 1/2.3-Type Exmor R High-speed, Low-noise CMOS Sensor | 20x optical zoom, f=4.4mm wide end to 88.4mm tele end, F2 to F3.8 | http://www.vaddio.com | 3840 x 2160 | North America | Over 50 dB | -20ø to +60ø C (-4øF to 140øF) | No | Vaddio UHD, 20x Zoom, North America, Silver PTZ Camera | 999-9950-000 | 20 | 20 |
| UHD, 20x Zoom, North America, White | Plastic - Vaddio - White | Plastic - Vaddio - White | 20% to 80% RH (non-condensing) | 1/2.3-Type Exmor R High-speed, Low-noise CMOS Sensor | 20x optical zoom, f=4.4mm wide end to 88.4mm tele end, F2 to F3.8 | http://www.vaddio.com | 3840 x 2160 | North America | Over 50 dB | -20ø to +60ø C (-4øF to 140øF) | No | Vaddio UHD, 20x Zoom, North America, White PTZ Camera | 999-9950-000W | 20 | 20 |
| UHD, 20x Zoom, Europe/UK, Silver | Plastic - Vaddio - Silver | Plastic - Vaddio - Black | 20% to 80% RH (non-condensing) | 1/2.3-Type Exmor R High-speed, Low-noise CMOS Sensor | 20x optical zoom, f=4.4mm wide end to 88.4mm tele end, F2 to F3.8 | http://www.vaddio.com | 3840 x 2160 | Europe/UK | Over 50 dB | -20ø to +60ø C (-4øF to 140øF) | No | Vaddio UHD, 20x Zoom, Europe/UK, Silver PTZ Camera | 999-9950-001 | 20 | 20 |
| UHD, 20x Zoom, Europe/UK, White | Plastic - Vaddio - White | Plastic - Vaddio - White | 20% to 80% RH (non-condensing) | 1/2.3-Type Exmor R High-speed, Low-noise CMOS Sensor | 20x optical zoom, f=4.4mm wide end to 88.4mm tele end, F2 to F3.8 | http://www.vaddio.com | 3840 x 2160 | Europe/UK | Over 50 dB | -20ø to +60ø C (-4øF to 140øF) | No | Vaddio UHD, 20x Zoom, Europe/UK, White PTZ Camera | 999-9950-001W | 20 | 20 |
| UHD, 20x Zoom, Australia/New Zealand, Silver | Plastic - Vaddio - Silver | Plastic - Vaddio - Black | 20% to 80% RH (non-condensing) | 1/2.3-Type Exmor R High-speed, Low-noise CMOS Sensor | 20x optical zoom, f=4.4mm wide end to 88.4mm tele end, F2 to F3.8 | http://www.vaddio.com | 3840 x 2160 | Australia/New Zealand | Over 50 dB | -20ø to +60ø C (-4øF to 140øF) | No | Vaddio UHD, 20x Zoom, Australia/New Zealand, Silver PTZ Camera | 999-9950-009 | 20 | 20 |
| UHD, 20x Zoom, Australia/New Zealand, White | Plastic - Vaddio - White | Plastic - Vaddio - White | 20% to 80% RH (non-condensing) | 1/2.3-Type Exmor R High-speed, Low-noise CMOS Sensor | 20x optical zoom, f=4.4mm wide end to 88.4mm tele end, F2 to F3.8 | http://www.vaddio.com | 3840 x 2160 | Australia/New Zealand | Over 50 dB | -20ø to +60ø C (-4øF to 140øF) | No | Vaddio UHD, 20x Zoom, Australia/New Zealand, White PTZ Camera | 999-9950-009W | 20 | 20 |
| USB, 12x Zoom, North America, Silver | Plastic - Vaddio - Silver | Plastic - Vaddio - Black | 20% to 80% non-condensing | 1/2.8-type Exmor CMOS sensor | 12X optical zoom, 73ø wide to 6.6ø tele, f=3.91 mm to 47 mm, F1.8 to F3.4 | http://www.vaddio.com | 1080 x 1920 | North America | Over 50 dB | -20øC to +60øC (-4øF to 140øF) | No | Vaddio USB, 12x Zoom, North America, Silver PTZ Camera | 999-9920-000 | 12 | 30 |
| USB, 12x Zoom, Europe/UK, Silver | Plastic - Vaddio - Silver | Plastic - Vaddio - Black | 20% to 80% non-condensing | 1/2.8-type Exmor CMOS sensor | 12X optical zoom, 73ø wide to 6.6ø tele, f=3.91 mm to 47 mm, F1.8 to F3.4 | http://www.vaddio.com | 1080 x 1920 | Europe/UK | Over 50 dB | -20øC to +60øC (-4øF to 140øF) | No | Vaddio USB, 12x Zoom, Europe/UK, Silver PTZ Camera | 999-9920-001 | 12 | 30 |
| USB, 12x Zoom, Australia/New Zealand, Silver | Plastic - Vaddio - Silver | Plastic - Vaddio - Black | 20% to 80% non-condensing | 1/2.8-type Exmor CMOS sensor | 12X optical zoom, 73ø wide to 6.6ø tele, f=3.91 mm to 47 mm, F1.8 to F3.4 | http://www.vaddio.com | 1080 x 1920 | Australia/New Zealand | Over 50 dB | -20øC to +60øC (-4øF to 140øF) | No | Vaddio USB, 12x Zoom, Australia/New Zealand, Silver PTZ Camera | 999-9920-009 | 12 | 30 |
| USB, 12x Zoom, North America, Elite, Black | Plastic - Vaddio - Black | Plastic - Vaddio - Black | 20% to 80% non-condensing | 1/2.8-type Exmor CMOS sensor | 12X optical zoom, 73ø wide to 6.6ø tele, f=3.91 mm to 47 mm, F1.8 to F3.4 |  | 1080 x 1920 | North America | Over 50 dB | -20øC to +60øC (-4øF to 140øF) | No | Vaddio USB, 12x Zoom, North America, Elite, Black PTZ Camera | 999-99200-000 | 12 | 30 |
| USB, 12x Zoom, North America, Elite, White | Plastic - Vaddio - White | Plastic - Vaddio - White | 20% to 80% non-condensing | 1/2.8-type Exmor CMOS sensor | 12X optical zoom, 73ø wide to 6.6ø tele, f=3.91 mm to 47 mm, F1.8 to F3.4 |  | 1080 x 1920 | North America | Over 50 dB | -20øC to +60øC (-4øF to 140øF) | No | Vaddio USB, 12x Zoom, North America, Elite, White PTZ Camera | 999-99200-000W | 12 | 30 |
| USB, 30x Zoom, North America, Elite, Black | Plastic - Vaddio - Black | Plastic - Vaddio - Black | 20% to 80% non-condensing | 1/2.8-type Exmor CMOS sensor | 30X optical zoom, 65ø (wide end) to 2.3ø (tele end), F1.6 to F4.7 |  | 1080 x 1920 | North America | Over 50 dB | -20øC to +60øC (-4øF to 140øF) | No | Vaddio USB, 30x Zoom, North America, Elite, Black PTZ Camera | 999-99230-000 | 30 | 30 |
| USB, 30x Zoom, North America, Elite, White | Plastic - Vaddio - White | Plastic - Vaddio - White | 20% to 80% non-condensing | 1/2.8-type Exmor CMOS sensor | 30X optical zoom, 65ø (wide end) to 2.3ø (tele end), F1.6 to F4.7 |  | 1080 x 1920 | North America | Over 50 dB | -20øC to +60øC (-4øF to 140øF) | No | Vaddio USB, 30x Zoom, North America, Elite, White PTZ Camera | 999-99230-000W | 30 | 30 |
| USB, 12x Zoom, Europe/UK, Elite, Black | Plastic - Vaddio - Black | Plastic - Vaddio - Black | 20% to 80% non-condensing | 1/2.8-type Exmor CMOS sensor | 12X optical zoom, 73ø wide to 6.6ø tele, f=3.91 mm to 47 mm, F1.8 to F3.4 |  | 1080 x 1920 | Europe/UK | Over 50 dB | -20øC to +60øC (-4øF to 140øF) | No | Vaddio USB, 12x Zoom, Europe/UK, Elite, Black PTZ Camera | 999-99200-001 | 12 | 30 |
| USB, 12x Zoom, Europe/UK, Elite, White | Plastic - Vaddio - White | Plastic - Vaddio - White | 20% to 80% non-condensing | 1/2.8-type Exmor CMOS sensor | 12X optical zoom, 73ø wide to 6.6ø tele, f=3.91 mm to 47 mm, F1.8 to F3.4 |  | 1080 x 1920 | Europe/UK | Over 50 dB | -20øC to +60øC (-4øF to 140øF) | No | Vaddio USB, 12x Zoom, Europe/UK, Elite, White PTZ Camera | 999-99200-001W | 12 | 30 |
| USB, 30x Zoom, Europe/UK, Elite, Black | Plastic - Vaddio - Black | Plastic - Vaddio - Black | 20% to 80% non-condensing | 1/2.8-type Exmor CMOS sensor | 30X optical zoom, 65ø (wide end) to 2.3ø (tele end), F1.6 to F4.7 |  | 1080 x 1920 | Europe/UK | Over 50 dB | -20øC to +60øC (-4øF to 140øF) | No | Vaddio USB, 30x Zoom, Europe/UK, Elite, Black PTZ Camera | 999-99230-001 | 30 | 30 |
| USB, 30x Zoom, Europe/UK, Elite, White | Plastic - Vaddio - White | Plastic - Vaddio - White | 20% to 80% non-condensing | 1/2.8-type Exmor CMOS sensor | 30X optical zoom, 65ø (wide end) to 2.3ø (tele end), F1.6 to F4.7 |  | 1080 x 1920 | Europe/UK | Over 50 dB | -20øC to +60øC (-4øF to 140øF) | No | Vaddio USB, 30x Zoom, Europe/UK, Elite, White PTZ Camera | 999-99230-001W | 30 | 30 |
| USB, 12x Zoom, Australia/New Zealand, Elite, Black | Plastic - Vaddio - Black | Plastic - Vaddio - Black | 20% to 80% non-condensing | 1/2.8-type Exmor CMOS sensor | 12X optical zoom, 73ø wide to 6.6ø tele, f=3.91 mm to 47 mm, F1.8 to F3.4 |  | 1080 x 1920 | Australia/New Zealand | Over 50 dB | -20øC to +60øC (-4øF to 140øF) | No | Vaddio USB, 12x Zoom, Australia/New Zealand, Elite, Black PTZ Camera | 999-99200-009 | 12 | 30 |
| USB, 12x Zoom, Australia/New Zealand, Elite, White | Plastic - Vaddio - White | Plastic - Vaddio - White | 20% to 80% non-condensing | 1/2.8-type Exmor CMOS sensor | 12X optical zoom, 73ø wide to 6.6ø tele, f=3.91 mm to 47 mm, F1.8 to F3.4 |  | 1080 x 1920 | Australia/New Zealand | Over 50 dB | -20øC to +60øC (-4øF to 140øF) | No | Vaddio USB, 12x Zoom, Australia/New Zealand, Elite, White PTZ Camera | 999-99200-009W | 12 | 30 |
| USB, 30x Zoom, Australia/New Zealand, Elite, Black | Plastic - Vaddio - Black | Plastic - Vaddio - Black | 20% to 80% non-condensing | 1/2.8-type Exmor CMOS sensor | 30X optical zoom, 65ø (wide end) to 2.3ø (tele end), F1.6 to F4.7 |  | 1080 x 1920 | Australia/New Zealand | Over 50 dB | -20øC to +60øC (-4øF to 140øF) | No | Vaddio USB, 30x Zoom, Australia/New Zealand, Elite, Black PTZ Camera | 999-99230-009 | 30 | 30 |
| USB, 30x Zoom, Australia/New Zealand, Elite, White | Plastic - Vaddio - White | Plastic - Vaddio - White | 20% to 80% non-condensing | 1/2.8-type Exmor CMOS sensor | 30X optical zoom, 65ø (wide end) to 2.3ø (tele end), F1.6 to F4.7 |  | 1080 x 1920 | Australia/New Zealand | Over 50 dB | -20øC to +60øC (-4øF to 140øF) | No | Vaddio USB, 30x Zoom, Australia/New Zealand, Elite, White PTZ Camera | 999-99230-009W | 30 | 30 |

## geometry (parser evidence)
native form markers: Blend x4, Sweep x12
no freeform markers — native parametric forms only
